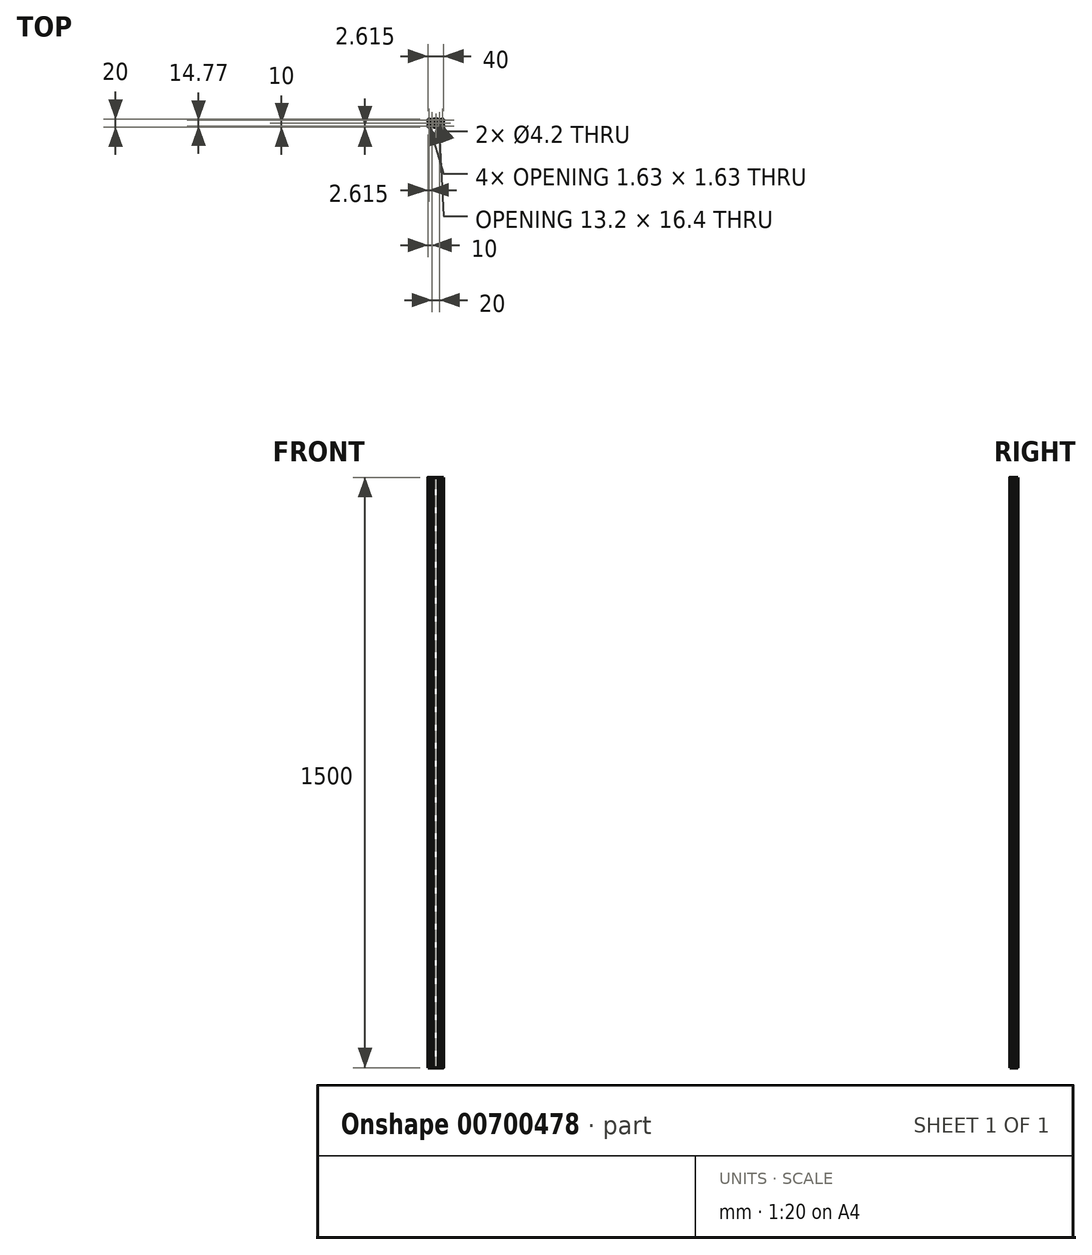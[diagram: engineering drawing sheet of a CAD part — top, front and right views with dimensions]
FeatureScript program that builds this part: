
annotation { "Feature Type Name" : "Feature", "Feature Type Description" : "" }
export const myFeature = defineFeature(function(context is Context, id is Id, definition is map)
    precondition{}
    {
        {
            var Q0;
            Q0=qCreatedBy(makeId("Top.planeOp"),FACE);
            var sketch = newSketch(context, id + "F0", { "sketchPlane" : qUnion([Q0])});
            skLineSegment(sketch, "E0", {"start": v(0, 0) * mm, "end": v(-3.5, 0) * mm, "construction": true});
            skLineSegment(sketch, "E1", {"start": v(0, 0) * mm, "end": v(0, -3.5) * mm, "construction": true});
            skLineSegment(sketch, "E2", {"start": v(0, 0) * mm, "end": v(-10, -10) * mm, "construction": true});
            skLineSegment(sketch, "E3", {"start": v(-3.5, -0.1) * mm, "end": v(-3.5, -2.44) * mm});
            skLineSegment(sketch, "E4", {"start": v(-3.5, -2.44) * mm, "end": v(-6.56, -5.5) * mm});
            skLineSegment(sketch, "E5", {"start": v(-6.56, -5.5) * mm, "end": v(-8.2, -5.5) * mm});
            skLineSegment(sketch, "E6", {"start": v(-8.2, -5.5) * mm, "end": v(-8.2, -2.9) * mm});
            skLineSegment(sketch, "E7", {"start": v(-8.2, -2.9) * mm, "end": v(-8.3, -2.9) * mm});
            skLineSegment(sketch, "E8", {"start": v(-8.3, -2.9) * mm, "end": v(-9.77, -4.35) * mm});
            skLineSegment(sketch, "E9", {"start": v(-10, -4.9) * mm, "end": v(-10, -8.5) * mm});
            skPoint(sketch, "E10.visualSharp", {"position": v(-10, -4.58) * mm});
            skArc(sketch, "E10.filletArc", {"start": v(-9.77, -4.35) * mm, "mid": v(-9.94, -4.6) * mm, "end": v(-10, -4.9) * mm});
            skLineSegment(sketch, "E11", {"start": v(-7.12, -7.12) * mm, "end": v(-7.66, -6.57) * mm});
            skLineSegment(sketch, "E12", {"start": v(-7.66, -6.57) * mm, "end": v(-8.2, -6.57) * mm});
            skLineSegment(sketch, "E13", {"start": v(-8.2, -6.57) * mm, "end": v(-8.2, -8.2) * mm});
            skLineSegment(sketch, "E14.MirrorCS", {"start": v(-4.9, -10) * mm, "end": v(-8.5, -10) * mm});
            skArc(sketch, "E15.MirrorCS", {"start": v(-4.35, -9.77) * mm, "mid": v(-4.6, -9.94) * mm, "end": v(-4.9, -10) * mm});
            skLineSegment(sketch, "E16.MirrorCS", {"start": v(-2.89, -8.3) * mm, "end": v(-4.35, -9.77) * mm});
            skLineSegment(sketch, "E17.MirrorCS", {"start": v(-5.5, -8.2) * mm, "end": v(-2.89, -8.2) * mm});
            skLineSegment(sketch, "E18.MirrorCS", {"start": v(-5.5, -6.56) * mm, "end": v(-5.5, -8.2) * mm});
            skLineSegment(sketch, "E19.MirrorCS", {"start": v(-2.44, -3.5) * mm, "end": v(-5.5, -6.56) * mm});
            skLineSegment(sketch, "E20.MirrorCS", {"start": v(-0.1, -3.5) * mm, "end": v(-2.44, -3.5) * mm});
            skLineSegment(sketch, "E21.MirrorCS", {"start": v(-6.57, -8.2) * mm, "end": v(-8.2, -8.2) * mm});
            skLineSegment(sketch, "E22.MirrorCS", {"start": v(-6.57, -7.66) * mm, "end": v(-6.57, -8.2) * mm});
            skLineSegment(sketch, "E23.MirrorCS", {"start": v(-7.11, -7.12) * mm, "end": v(-6.57, -7.66) * mm});
            skPoint(sketch, "E24.visualSharp", {"position": v(-10, -10) * mm});
            skArc(sketch, "E24.filletArc", {"start": v(-10, -8.5) * mm, "mid": v(-9.56, -9.56) * mm, "end": v(-8.5, -10) * mm});
            skLineSegment(sketch, "E25.MirrorCS", {"start": v(-2.89, -8.2) * mm, "end": v(-2.89, -8.3) * mm});
            skLineSegment(sketch, "E26.MirrorCS", {"start": v(0.1, -3.5) * mm, "end": v(2.44, -3.5) * mm});
            skLineSegment(sketch, "E27.MirrorCS", {"start": v(2.44, -3.5) * mm, "end": v(5.5, -6.56) * mm});
            skLineSegment(sketch, "E28.MirrorCS", {"start": v(5.5, -6.56) * mm, "end": v(5.5, -8.2) * mm});
            skLineSegment(sketch, "E29.MirrorCS", {"start": v(2.89, -8.2) * mm, "end": v(2.89, -8.3) * mm});
            skLineSegment(sketch, "E30.MirrorCS", {"start": v(2.89, -8.3) * mm, "end": v(4.35, -9.77) * mm});
            skLineSegment(sketch, "E31.MirrorCS", {"start": v(5.5, -8.2) * mm, "end": v(2.89, -8.2) * mm});
            skArc(sketch, "E32.MirrorCS", {"start": v(4.35, -9.77) * mm, "mid": v(4.6, -9.94) * mm, "end": v(4.9, -10) * mm});
            skLineSegment(sketch, "E33.MirrorCS", {"start": v(3.5, -0.1) * mm, "end": v(3.5, -2.44) * mm});
            skLineSegment(sketch, "E34.MirrorCS", {"start": v(0.1, 3.5) * mm, "end": v(2.44, 3.5) * mm});
            skLineSegment(sketch, "E35.MirrorCS", {"start": v(2.89, 8.2) * mm, "end": v(2.89, 8.3) * mm});
            skArc(sketch, "E36.MirrorCS", {"start": v(4.35, 9.77) * mm, "mid": v(4.6, 9.94) * mm, "end": v(4.9, 10) * mm});
            skLineSegment(sketch, "E37.MirrorCS", {"start": v(5.5, 6.56) * mm, "end": v(5.5, 8.2) * mm});
            skLineSegment(sketch, "E38.MirrorCS", {"start": v(2.44, 3.5) * mm, "end": v(5.5, 6.56) * mm});
            skLineSegment(sketch, "E39.MirrorCS", {"start": v(5.5, 8.2) * mm, "end": v(2.89, 8.2) * mm});
            skLineSegment(sketch, "E40.MirrorCS", {"start": v(2.89, 8.3) * mm, "end": v(4.35, 9.77) * mm});
            skLineSegment(sketch, "E41.MirrorCS", {"start": v(3.5, 0.1) * mm, "end": v(3.5, 2.44) * mm});
            skLineSegment(sketch, "E42.MirrorCS", {"start": v(-2.89, 8.2) * mm, "end": v(-2.89, 8.3) * mm});
            skLineSegment(sketch, "E43.MirrorCS", {"start": v(-5.5, 6.56) * mm, "end": v(-5.5, 8.2) * mm});
            skArc(sketch, "E44.MirrorCS", {"start": v(-4.35, 9.77) * mm, "mid": v(-4.6, 9.94) * mm, "end": v(-4.9, 10) * mm});
            skLineSegment(sketch, "E45.MirrorCS", {"start": v(-4.9, 10) * mm, "end": v(-8.5, 10) * mm});
            skLineSegment(sketch, "E46.MirrorCS", {"start": v(-2.89, 8.3) * mm, "end": v(-4.35, 9.77) * mm});
            skLineSegment(sketch, "E47.MirrorCS", {"start": v(-5.5, 8.2) * mm, "end": v(-2.89, 8.2) * mm});
            skLineSegment(sketch, "E48.MirrorCS", {"start": v(-2.44, 3.5) * mm, "end": v(-5.5, 6.56) * mm});
            skLineSegment(sketch, "E49.MirrorCS", {"start": v(-0.1, 3.5) * mm, "end": v(-2.44, 3.5) * mm});
            skLineSegment(sketch, "E50.MirrorCS", {"start": v(-3.5, 0.1) * mm, "end": v(-3.5, 2.44) * mm});
            skLineSegment(sketch, "E51.MirrorCS", {"start": v(-3.5, 2.44) * mm, "end": v(-6.56, 5.5) * mm});
            skLineSegment(sketch, "E52.MirrorCS", {"start": v(-6.56, 5.5) * mm, "end": v(-8.2, 5.5) * mm});
            skLineSegment(sketch, "E53.MirrorCS", {"start": v(-8.2, 2.9) * mm, "end": v(-8.3, 2.9) * mm});
            skLineSegment(sketch, "E54.MirrorCS", {"start": v(-8.2, 5.5) * mm, "end": v(-8.2, 2.9) * mm});
            skLineSegment(sketch, "E55.MirrorCS", {"start": v(-8.3, 2.9) * mm, "end": v(-9.77, 4.35) * mm});
            skLineSegment(sketch, "E56.MirrorCS", {"start": v(-6.57, 7.66) * mm, "end": v(-6.57, 8.2) * mm});
            skLineSegment(sketch, "E57.MirrorCS", {"start": v(-6.57, 8.2) * mm, "end": v(-8.2, 8.2) * mm});
            skLineSegment(sketch, "E58.MirrorCS", {"start": v(-7.11, 7.12) * mm, "end": v(-6.57, 7.66) * mm});
            skLineSegment(sketch, "E59.MirrorCS", {"start": v(-7.12, 7.12) * mm, "end": v(-7.66, 6.57) * mm});
            skLineSegment(sketch, "E60.MirrorCS", {"start": v(-7.66, 6.57) * mm, "end": v(-8.2, 6.57) * mm});
            skLineSegment(sketch, "E61.MirrorCS", {"start": v(-8.2, 6.57) * mm, "end": v(-8.2, 8.2) * mm});
            skArc(sketch, "E62.MirrorCS", {"start": v(-9.77, 4.35) * mm, "mid": v(-9.94, 4.6) * mm, "end": v(-10, 4.9) * mm});
            skArc(sketch, "E63.MirrorCS", {"start": v(-10, 8.5) * mm, "mid": v(-9.56, 9.56) * mm, "end": v(-8.5, 10) * mm});
            skLineSegment(sketch, "E64.MirrorCS", {"start": v(-10, 4.9) * mm, "end": v(-10, 8.5) * mm});
            skCircle(sketch, "E65", {"center": v(0, 0) * mm, "radius": 2.1 * mm});
            skLineSegment(sketch, "E66", {"start": v(-3.5, -0.1) * mm, "end": v(-3.4, 0) * mm});
            skLineSegment(sketch, "E67.MirrorCS", {"start": v(-3.5, 0.1) * mm, "end": v(-3.4, 0) * mm});
            skPoint(sketch, "E68.orphan", {"position": v(-3.5, 0) * mm});
            skLineSegment(sketch, "E69.MirrorCS", {"start": v(-0.1, -3.5) * mm, "end": v(0, -3.4) * mm});
            skLineSegment(sketch, "E70.MirrorCS", {"start": v(0.1, -3.5) * mm, "end": v(0, -3.4) * mm});
            skLineSegment(sketch, "E71.MirrorCS", {"start": v(0.1, 3.5) * mm, "end": v(0, 3.4) * mm});
            skLineSegment(sketch, "E72.MirrorCS", {"start": v(-0.1, 3.5) * mm, "end": v(0, 3.4) * mm});
            skLineSegment(sketch, "E73.MirrorCS", {"start": v(3.5, 0.1) * mm, "end": v(3.4, 0) * mm});
            skLineSegment(sketch, "E74.MirrorCS", {"start": v(3.5, -0.1) * mm, "end": v(3.4, 0) * mm});
            skPoint(sketch, "E75.orphan", {"position": v(0, -3.5) * mm});
            skPoint(sketch, "E76.orphan", {"position": v(3.5, 0) * mm});
            skPoint(sketch, "E77.orphan", {"position": v(0, 3.5) * mm});
            skLineSegment(sketch, "E78", {"start": v(3.5, -2.44) * mm, "end": v(6.9, -5.84) * mm});
            skLineSegment(sketch, "E79", {"start": v(6.9, -5.84) * mm, "end": v(6.9, -8.2) * mm});
            skLineSegment(sketch, "E80", {"start": v(6.9, -8.2) * mm, "end": v(10, -8.2) * mm});
            skLineSegment(sketch, "E81", {"start": v(4.9, -10) * mm, "end": v(10, -10) * mm});
            skLineSegment(sketch, "E82.MirrorCS", {"start": v(4.9, 10) * mm, "end": v(10, 10) * mm});
            skLineSegment(sketch, "E83.MirrorCS", {"start": v(6.9, 8.2) * mm, "end": v(10, 8.2) * mm});
            skLineSegment(sketch, "E84.MirrorCS", {"start": v(6.9, 5.84) * mm, "end": v(6.9, 8.2) * mm});
            skLineSegment(sketch, "E85.MirrorCS", {"start": v(3.5, 2.44) * mm, "end": v(6.9, 5.84) * mm});
            skLineSegment(sketch, "E86", {"start": v(10, 10) * mm, "end": v(10, -10) * mm, "construction": true});
            skLineSegment(sketch, "E87.MirrorCS", {"start": v(15.1, -10) * mm, "end": v(10, -10) * mm});
            skLineSegment(sketch, "E88.MirrorCS", {"start": v(13.1, -8.2) * mm, "end": v(10, -8.2) * mm});
            skLineSegment(sketch, "E89.MirrorCS", {"start": v(13.1, -5.84) * mm, "end": v(13.1, -8.2) * mm});
            skLineSegment(sketch, "E90.MirrorCS", {"start": v(16.5, -2.44) * mm, "end": v(13.1, -5.84) * mm});
            skArc(sketch, "E91.MirrorCS", {"start": v(15.65, -9.77) * mm, "mid": v(15.4, -9.94) * mm, "end": v(15.1, -10) * mm});
            skLineSegment(sketch, "E92.MirrorCS", {"start": v(16.5, -0.1) * mm, "end": v(16.5, -2.44) * mm});
            skLineSegment(sketch, "E93.MirrorCS", {"start": v(16.5, 0.1) * mm, "end": v(16.5, 2.44) * mm});
            skLineSegment(sketch, "E94.MirrorCS", {"start": v(16.5, 2.44) * mm, "end": v(13.1, 5.84) * mm});
            skLineSegment(sketch, "E95.MirrorCS", {"start": v(13.1, 5.84) * mm, "end": v(13.1, 8.2) * mm});
            skLineSegment(sketch, "E96.MirrorCS", {"start": v(13.1, 8.2) * mm, "end": v(10, 8.2) * mm});
            skLineSegment(sketch, "E97.MirrorCS", {"start": v(15.1, 10) * mm, "end": v(10, 10) * mm});
            skArc(sketch, "E98.MirrorCS", {"start": v(15.65, 9.77) * mm, "mid": v(15.4, 9.94) * mm, "end": v(15.1, 10) * mm});
            skLineSegment(sketch, "E99.MirrorCS", {"start": v(17.11, 8.31) * mm, "end": v(15.65, 9.77) * mm});
            skLineSegment(sketch, "E100.MirrorCS", {"start": v(14.5, 8.2) * mm, "end": v(17.1, 8.2) * mm});
            skLineSegment(sketch, "E101.MirrorCS", {"start": v(14.5, 6.56) * mm, "end": v(14.5, 8.2) * mm});
            skLineSegment(sketch, "E102.MirrorCS", {"start": v(17.56, 3.5) * mm, "end": v(14.5, 6.56) * mm});
            skLineSegment(sketch, "E103.MirrorCS", {"start": v(17.56, -3.5) * mm, "end": v(14.5, -6.56) * mm});
            skLineSegment(sketch, "E104.MirrorCS", {"start": v(14.5, -6.56) * mm, "end": v(14.5, -8.2) * mm});
            skLineSegment(sketch, "E105.MirrorCS", {"start": v(14.5, -8.2) * mm, "end": v(17.11, -8.2) * mm});
            skLineSegment(sketch, "E106.MirrorCS", {"start": v(17.11, -8.31) * mm, "end": v(15.65, -9.77) * mm});
            skLineSegment(sketch, "E107.MirrorCS", {"start": v(16.5, 0.1) * mm, "end": v(16.6, 0) * mm});
            skLineSegment(sketch, "E108.MirrorCS", {"start": v(16.5, -0.1) * mm, "end": v(16.6, 0) * mm});
            skCircle(sketch, "E109.MirrorC", {"center": v(20, 0) * mm, "radius": 2.1 * mm});
            skLineSegment(sketch, "E110.MirrorCS", {"start": v(19.9, 3.5) * mm, "end": v(17.56, 3.5) * mm});
            skLineSegment(sketch, "E111.MirrorCS", {"start": v(19.9, -3.5) * mm, "end": v(17.56, -3.5) * mm});
            skLineSegment(sketch, "E112.MirrorCS", {"start": v(20.1, -3.5) * mm, "end": v(22.44, -3.5) * mm});
            skLineSegment(sketch, "E113.MirrorCS", {"start": v(20.1, 3.5) * mm, "end": v(22.44, 3.5) * mm});
            skLineSegment(sketch, "E114.MirrorCS", {"start": v(20.1, 3.5) * mm, "end": v(20, 3.4) * mm});
            skLineSegment(sketch, "E115.MirrorCS", {"start": v(19.9, 3.5) * mm, "end": v(20, 3.4) * mm});
            skLineSegment(sketch, "E116.MirrorCS", {"start": v(19.9, -3.5) * mm, "end": v(20, -3.4) * mm});
            skLineSegment(sketch, "E117.MirrorCS", {"start": v(20.1, -3.5) * mm, "end": v(20, -3.4) * mm});
            skLineSegment(sketch, "E118.MirrorCS", {"start": v(22.44, -3.5) * mm, "end": v(25.5, -6.56) * mm});
            skLineSegment(sketch, "E119.MirrorCS", {"start": v(25.5, -6.56) * mm, "end": v(25.5, -8.2) * mm});
            skLineSegment(sketch, "E120.MirrorCS", {"start": v(25.5, -8.2) * mm, "end": v(22.9, -8.2) * mm});
            skLineSegment(sketch, "E121.MirrorCS", {"start": v(17.11, -8.2) * mm, "end": v(17.11, -8.3) * mm});
            skLineSegment(sketch, "E122.MirrorCS", {"start": v(17.11, 8.2) * mm, "end": v(17.11, 8.31) * mm});
            skLineSegment(sketch, "E123.MirrorCS", {"start": v(22.89, -8.2) * mm, "end": v(22.89, -8.3) * mm});
            skLineSegment(sketch, "E124.MirrorCS", {"start": v(22.89, -8.31) * mm, "end": v(24.35, -9.77) * mm});
            skArc(sketch, "E125.MirrorCS", {"start": v(24.35, -9.77) * mm, "mid": v(24.6, -9.94) * mm, "end": v(24.9, -10) * mm});
            skLineSegment(sketch, "E126.MirrorCS", {"start": v(24.9, -10) * mm, "end": v(28.5, -10) * mm});
            skArc(sketch, "E127.MirrorCS", {"start": v(30, -8.5) * mm, "mid": v(29.56, -9.56) * mm, "end": v(28.5, -10) * mm});
            skLineSegment(sketch, "E128.MirrorCS", {"start": v(30, -4.9) * mm, "end": v(30, -8.5) * mm});
            skArc(sketch, "E129.MirrorCS", {"start": v(29.77, -4.35) * mm, "mid": v(29.94, -4.6) * mm, "end": v(30, -4.9) * mm});
            skLineSegment(sketch, "E130.MirrorCS", {"start": v(28.3, -2.9) * mm, "end": v(29.77, -4.35) * mm});
            skLineSegment(sketch, "E131.MirrorCS", {"start": v(28.2, -2.89) * mm, "end": v(28.31, -2.89) * mm});
            skLineSegment(sketch, "E132.MirrorCS", {"start": v(28.2, -5.5) * mm, "end": v(28.2, -2.89) * mm});
            skLineSegment(sketch, "E133.MirrorCS", {"start": v(27.66, -6.57) * mm, "end": v(28.2, -6.57) * mm});
            skLineSegment(sketch, "E134.MirrorCS", {"start": v(27.12, -7.11) * mm, "end": v(27.66, -6.57) * mm});
            skLineSegment(sketch, "E135.MirrorCS", {"start": v(28.2, -6.57) * mm, "end": v(28.2, -8.2) * mm});
            skLineSegment(sketch, "E136.MirrorCS", {"start": v(26.57, -8.2) * mm, "end": v(28.2, -8.2) * mm});
            skLineSegment(sketch, "E137.MirrorCS", {"start": v(26.57, -7.66) * mm, "end": v(26.57, -8.2) * mm});
            skLineSegment(sketch, "E138.MirrorCS", {"start": v(27.12, -7.11) * mm, "end": v(26.57, -7.66) * mm});
            skLineSegment(sketch, "E139.MirrorCS", {"start": v(26.56, -5.5) * mm, "end": v(28.2, -5.5) * mm});
            skLineSegment(sketch, "E140.MirrorCS", {"start": v(23.5, -2.44) * mm, "end": v(26.56, -5.5) * mm});
            skLineSegment(sketch, "E141.MirrorCS", {"start": v(23.5, -0.1) * mm, "end": v(23.5, -2.44) * mm});
            skLineSegment(sketch, "E142.MirrorCS", {"start": v(23.5, 0.1) * mm, "end": v(23.5, 2.44) * mm});
            skLineSegment(sketch, "E143.MirrorCS", {"start": v(23.5, 0.1) * mm, "end": v(23.4, 0) * mm});
            skLineSegment(sketch, "E144.MirrorCS", {"start": v(23.5, -0.1) * mm, "end": v(23.4, 0) * mm});
            skLineSegment(sketch, "E145.MirrorCS", {"start": v(23.5, 2.44) * mm, "end": v(26.56, 5.5) * mm});
            skLineSegment(sketch, "E146.MirrorCS", {"start": v(22.44, 3.5) * mm, "end": v(25.5, 6.56) * mm});
            skLineSegment(sketch, "E147.MirrorCS", {"start": v(25.5, 6.56) * mm, "end": v(25.5, 8.2) * mm});
            skLineSegment(sketch, "E148.MirrorCS", {"start": v(26.56, 5.5) * mm, "end": v(28.2, 5.5) * mm});
            skLineSegment(sketch, "E149.MirrorCS", {"start": v(27.12, 7.11) * mm, "end": v(27.66, 6.57) * mm});
            skLineSegment(sketch, "E150.MirrorCS", {"start": v(27.12, 7.11) * mm, "end": v(26.57, 7.66) * mm});
            skLineSegment(sketch, "E151.MirrorCS", {"start": v(27.66, 6.57) * mm, "end": v(28.2, 6.57) * mm});
            skLineSegment(sketch, "E152.MirrorCS", {"start": v(26.57, 7.66) * mm, "end": v(26.57, 8.2) * mm});
            skLineSegment(sketch, "E153.MirrorCS", {"start": v(26.57, 8.2) * mm, "end": v(28.2, 8.2) * mm});
            skLineSegment(sketch, "E154.MirrorCS", {"start": v(28.2, 6.57) * mm, "end": v(28.2, 8.2) * mm});
            skLineSegment(sketch, "E155.MirrorCS", {"start": v(25.5, 8.2) * mm, "end": v(22.9, 8.2) * mm});
            skLineSegment(sketch, "E156.MirrorCS", {"start": v(28.2, 5.5) * mm, "end": v(28.2, 2.9) * mm});
            skLineSegment(sketch, "E157.MirrorCS", {"start": v(28.2, 2.9) * mm, "end": v(28.31, 2.9) * mm});
            skArc(sketch, "E158.MirrorCS", {"start": v(30, 8.5) * mm, "mid": v(29.56, 9.56) * mm, "end": v(28.5, 10) * mm});
            skLineSegment(sketch, "E159.MirrorCS", {"start": v(30, 4.9) * mm, "end": v(30, 8.5) * mm});
            skArc(sketch, "E160.MirrorCS", {"start": v(29.77, 4.35) * mm, "mid": v(29.94, 4.6) * mm, "end": v(30, 4.9) * mm});
            skLineSegment(sketch, "E161.MirrorCS", {"start": v(24.9, 10) * mm, "end": v(28.5, 10) * mm});
            skArc(sketch, "E162.MirrorCS", {"start": v(24.35, 9.77) * mm, "mid": v(24.6, 9.94) * mm, "end": v(24.9, 10) * mm});
            skLineSegment(sketch, "E163.MirrorCS", {"start": v(22.89, 8.31) * mm, "end": v(24.35, 9.77) * mm});
            skLineSegment(sketch, "E164.MirrorCS", {"start": v(28.3, 2.9) * mm, "end": v(29.77, 4.35) * mm});
            skLineSegment(sketch, "E165.MirrorCS", {"start": v(22.89, 8.2) * mm, "end": v(22.89, 8.31) * mm});
            skSolve(sketch);
        }
        {
            var Q0;
            Q0=qSketchRegion(id+"F0",true);
            extrude(context, id + "F1", {"entities" : qUnion([Q0]), "depth" : 1500 * mm});
        }
    });
